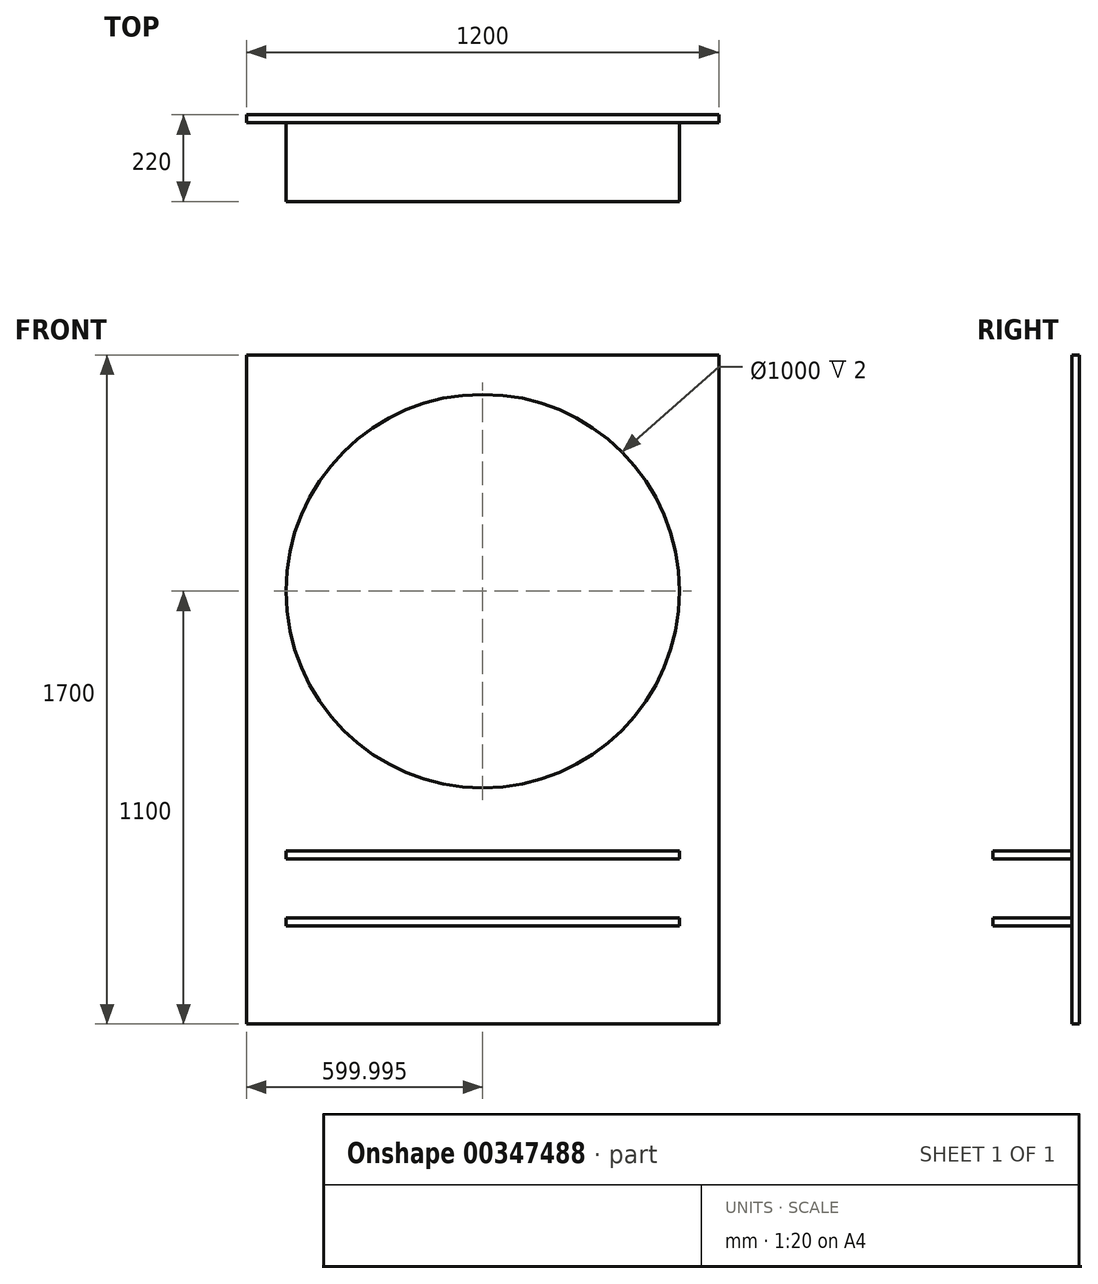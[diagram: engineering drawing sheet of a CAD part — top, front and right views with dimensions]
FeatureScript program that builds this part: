
annotation { "Feature Type Name" : "Feature", "Feature Type Description" : "" }
export const myFeature = defineFeature(function(context is Context, id is Id, definition is map)
    precondition{}
    {
        {
            var Q0;
            Q0=qCreatedBy(makeId("Front.planeOp"),FACE);
            var sketch = newSketch(context, id + "F0", { "sketchPlane" : qUnion([Q0])});
            skLineSegment(sketch, "E0.bottom", {"start": v(-33.1, 1641.88) * mm, "end": v(1166.9, 1641.88) * mm});
            skLineSegment(sketch, "E0.top", {"start": v(-33.1, -58.12) * mm, "end": v(1166.9, -58.12) * mm});
            skLineSegment(sketch, "E0.left", {"start": v(-33.1, 1641.88) * mm, "end": v(-33.1, -58.12) * mm});
            skLineSegment(sketch, "E0.right", {"start": v(1166.9, 1641.88) * mm, "end": v(1166.9, -58.12) * mm});
            skSolve(sketch);
        }
        {
            var Q0;
            Q0 = qSketchRegion(id + "F0", true);
            extrude(context, id + "F1", {"entities" : qUnion([Q0]), "depth" : 20 * mm});
        }
        {
            var Q0;
            Q0=makeQuery(id+"F1.opExtrude","CAP_FACE",FACE,{"disambiguationData":[OSD([sQuery(id+"F0.wireOp",EDGE,"E0.bottom"),sQuery(id+"F0.wireOp",EDGE,"E0.top"),sQuery(id+"F0.wireOp",EDGE,"E0.left"),sQuery(id+"F0.wireOp",EDGE,"E0.right")])],"isStart":false});
            var sketch = newSketch(context, id + "F2", { "sketchPlane" : qUnion([Q0])});
            skCircle(sketch, "E1", {"center": v(566.9, 1041.88) * mm, "radius": 500 * mm});
            skPoint(sketch, "E2.start.orphan", {"position": v(566.9, 1641.88) * mm});
            skPoint(sketch, "E3.orphan", {"position": v(566.9, 1541.88) * mm});
            skPoint(sketch, "E4.end.orphan", {"position": v(566.9, 541.88) * mm});
            skSolve(sketch);
        }
        {
            var Q0;
            Q0 = qSketchRegion(id + "F2", true);
            extrude(context, id + "F3", {"entities" : qUnion([Q0]), "operationType" : NewBodyOperationType.REMOVE, "oppositeDirection" : true, "depth" : 2 * mm});
        }
        {
            var Q0;
            Q0=makeQuery(id+"F1.opExtrude","CAP_FACE",FACE,{"disambiguationData":[OSD([sQuery(id+"F0.wireOp",EDGE,"E0.bottom"),sQuery(id+"F0.wireOp",EDGE,"E0.top"),sQuery(id+"F0.wireOp",EDGE,"E0.left"),sQuery(id+"F0.wireOp",EDGE,"E0.right")])],"isStart":false});
            var sketch = newSketch(context, id + "F4", { "sketchPlane" : qUnion([Q0])});
            skLineSegment(sketch, "E5", {"start": v(566.9, 191.88) * mm, "end": v(66.9, 191.88) * mm});
            skLineSegment(sketch, "E6", {"start": v(566.9, 191.88) * mm, "end": v(1066.9, 191.88) * mm});
            skLineSegment(sketch, "E7", {"start": v(66.9, 191.88) * mm, "end": v(66.9, 211.88) * mm});
            skLineSegment(sketch, "E8", {"start": v(66.9, 211.88) * mm, "end": v(1066.9, 211.88) * mm});
            skLineSegment(sketch, "E9", {"start": v(1066.9, 211.88) * mm, "end": v(1066.9, 191.88) * mm});
            skLineSegment(sketch, "E10.bottom", {"start": v(66.9, 361.88) * mm, "end": v(1066.9, 361.88) * mm});
            skLineSegment(sketch, "E10.top", {"start": v(66.9, 381.88) * mm, "end": v(1066.9, 381.88) * mm});
            skLineSegment(sketch, "E10.left", {"start": v(66.9, 361.88) * mm, "end": v(66.9, 381.88) * mm});
            skLineSegment(sketch, "E10.right", {"start": v(1066.9, 361.88) * mm, "end": v(1066.9, 381.88) * mm});
            skPoint(sketch, "E11.end.orphan", {"position": v(566.9, 361.88) * mm});
            skPoint(sketch, "E11.start.orphan", {"position": v(566.9, 211.88) * mm});
            skPoint(sketch, "E12.start.orphan", {"position": v(566.9, -58.12) * mm});
            skSolve(sketch);
        }
        {
            var Q0;
            Q0 = qSketchRegion(id + "F4", true);
            extrude(context, id + "F5", {"entities" : qUnion([Q0]), "operationType" : NewBodyOperationType.ADD, "depth" : 200 * mm});
        }
    });
